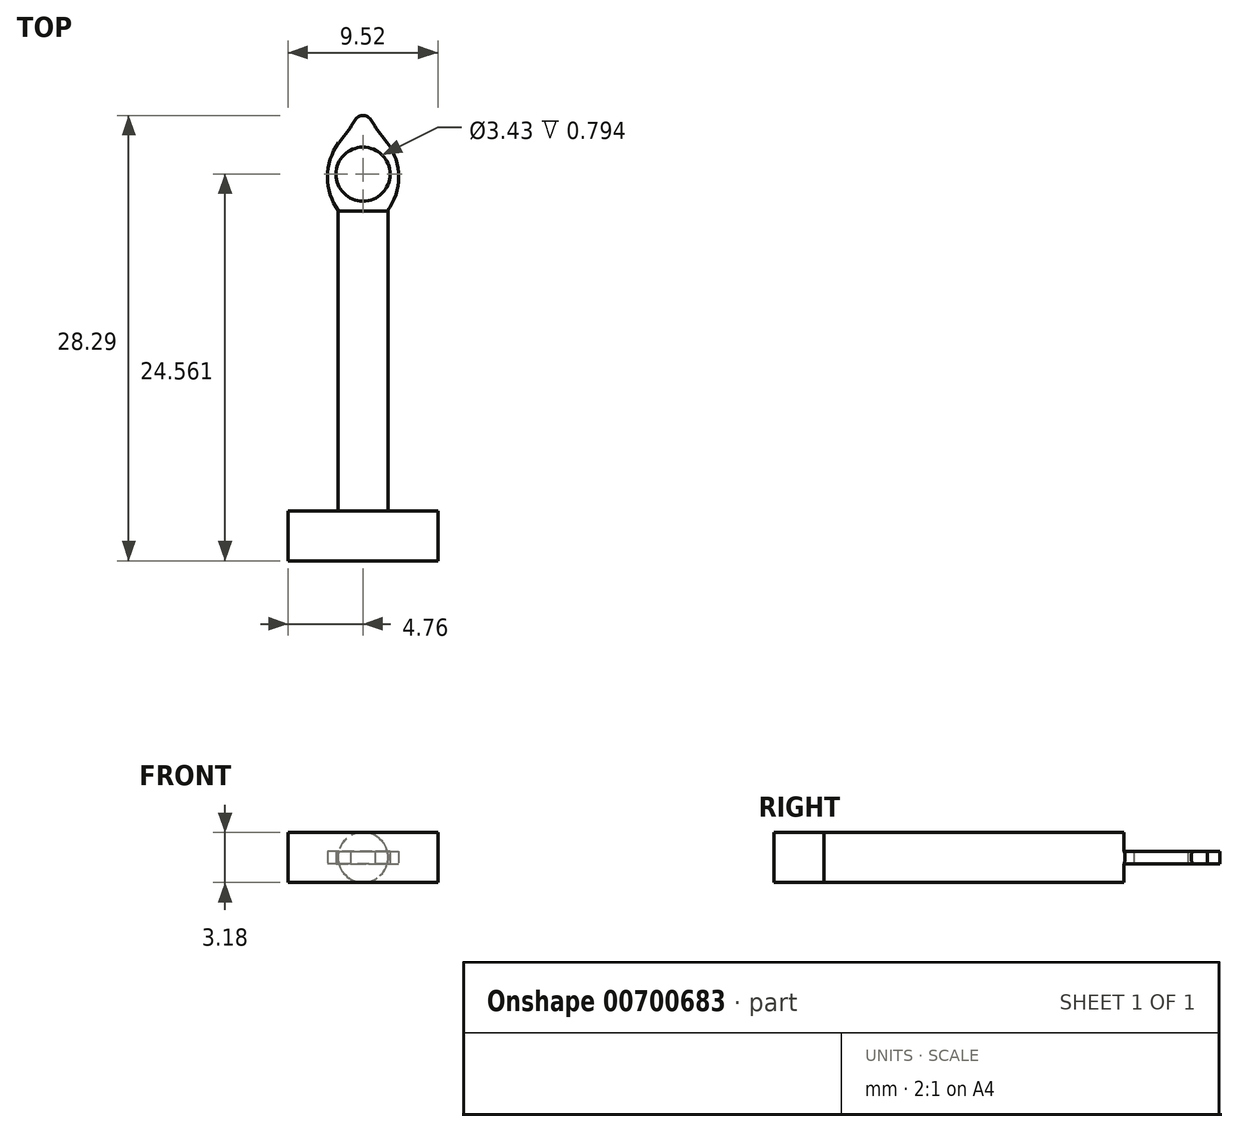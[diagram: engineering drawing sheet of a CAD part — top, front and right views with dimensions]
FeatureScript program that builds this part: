
annotation { "Feature Type Name" : "Feature", "Feature Type Description" : "" }
export const myFeature = defineFeature(function(context is Context, id is Id, definition is map)
    precondition{}
    {
        {
            var Q0;
            Q0=qCreatedBy(makeId("Front.planeOp"),FACE);
            var sketch = newSketch(context, id + "F0", { "sketchPlane" : qUnion([Q0])});
            skCircle(sketch, "E0", {"center": v(0, 0) * mm, "radius": 1.59 * mm});
            skSolve(sketch);
        }
        {
            var Q0;
            Q0 = qSketchRegion(id + "F0", true);
            extrude(context, id + "F1", {"entities" : qUnion([Q0]), "depth" : 25.4 * mm, "offsetDistance" : 25.4 * mm});
        }
        {
            var Q0;
            Q0=makeQuery(id+"F1.opExtrude","CAP_FACE",FACE,{"disambiguationData":[OSD([sQuery(id+"F0.wireOp",EDGE,"E0")])],"isStart":false});
            var sketch = newSketch(context, id + "F2", { "sketchPlane" : qUnion([Q0])});
            skLineSegment(sketch, "E1.bottom", {"start": v(-4.76, 1.59) * mm, "end": v(4.76, 1.59) * mm});
            skLineSegment(sketch, "E1.top", {"start": v(-4.76, -1.59) * mm, "end": v(4.76, -1.59) * mm});
            skLineSegment(sketch, "E1.left", {"start": v(-4.76, 1.59) * mm, "end": v(-4.76, -1.59) * mm});
            skLineSegment(sketch, "E1.right", {"start": v(4.76, 1.59) * mm, "end": v(4.76, -1.59) * mm});
            skPoint(sketch, "E2", {"position": v(0, 1.59) * mm});
            skPoint(sketch, "E3", {"position": v(0, -1.59) * mm});
            skSolve(sketch);
        }
        {
            var Q0;
            Q0 = qSketchRegion(id + "F2", true);
            extrude(context, id + "F3", {"entities" : qUnion([Q0]), "operationType" : NewBodyOperationType.ADD, "depth" : 3.17 * mm, "offsetDistance" : 25.4 * mm});
        }
        {
            var Q0;
            Q0=makeQuery(id+"F1.opExtrude","CAP_FACE",FACE,{"disambiguationData":[OSD([sQuery(id+"F0.wireOp",EDGE,"E0")])],"isStart":true});
            var sketch = newSketch(context, id + "F4", { "sketchPlane" : qUnion([Q0])});
            skLineSegment(sketch, "E4", {"start": v(1.54, 0.4) * mm, "end": v(-1.54, 0.4) * mm});
            skLineSegment(sketch, "E5", {"start": v(-1.54, -0.4) * mm, "end": v(1.54, -0.4) * mm});
            skArc(sketch, "E6.0", {"start": v(1.54, 0.4) * mm, "mid": v(0, 1.59) * mm, "end": v(-1.54, 0.4) * mm});
            skArc(sketch, "E7.trimOffspring", {"start": v(-1.54, -0.4) * mm, "mid": v(0, -1.59) * mm, "end": v(1.54, -0.4) * mm});
            skSolve(sketch);
        }
        {
            var Q0;
            Q0 = qSketchRegion(id + "F4", true);
            extrude(context, id + "F5", {"entities" : qUnion([Q0]), "operationType" : NewBodyOperationType.REMOVE, "oppositeDirection" : true, "depth" : 6.35 * mm, "offsetDistance" : 25.4 * mm});
        }
        {
            var Q0;
            Q0=makeQuery(id+"F5.boolean.opBoolean","COPY",FACE,{"derivedFrom":makeQuery(id+"F5.opExtrude","SWEPT_FACE",FACE,{"disambiguationData":[OSD([sQuery(id+"F4.wireOp",EDGE,"E5")])]})});
            var sketch = newSketch(context, id + "F6", { "sketchPlane" : qUnion([Q0])});
            skPoint(sketch, "E8", {"position": v(1.54, 2.02) * mm});
            skPoint(sketch, "E9", {"position": v(-1.54, 2.02) * mm});
            skLineSegment(sketch, "E10", {"start": v(0, 0) * mm, "end": v(1.54, 2.02) * mm});
            skLineSegment(sketch, "E11", {"start": v(0, 0) * mm, "end": v(-1.54, 2.02) * mm});
            skLineSegment(sketch, "E12", {"start": v(1.54, 2.02) * mm, "end": v(2.9, 3.82) * mm});
            skLineSegment(sketch, "E13", {"start": v(-1.54, 2.02) * mm, "end": v(-2.9, 3.82) * mm});
            skLineSegment(sketch, "E14", {"start": v(-2.9, 3.82) * mm, "end": v(-2.9, -0.78) * mm});
            skLineSegment(sketch, "E15", {"start": v(-2.9, -0.78) * mm, "end": v(2.9, -0.78) * mm});
            skLineSegment(sketch, "E16", {"start": v(2.9, -0.78) * mm, "end": v(2.9, 3.82) * mm});
            skSolve(sketch);
        }
        {
            var Q0;
            Q0 = qSketchRegion(id + "F6", true);
            extrude(context, id + "F7", {"entities" : qUnion([Q0]), "operationType" : NewBodyOperationType.REMOVE, "oppositeDirection" : true, "depth" : 25.4 * mm, "offsetDistance" : 25.4 * mm});
        }
        {
            var Q0;
            Q0=makeQuery(id+"F7.boolean.opBoolean","COPY",EDGE,{"derivedFrom":makeQuery(id+"F7.opExtrude","SWEPT_EDGE",EDGE,{"disambiguationData":[OSD([sQuery(id+"F4.wireOp",EDGE,"E5"),sQuery(id+"F6.wireOp",EDGE,"E10"),sQuery(id+"F6.wireOp",EDGE,"E11")])]})});
            fillet(context, id + "F8", {"entities" : qUnion([Q0]), "radius" : 1.02 * mm, "tangentPropagation" : true, "rho" : 0.5, "crossSection" : FilletCrossSection.CONIC, "allowEdgeOverflow" : false});
        }
        {
            var Q0;
            Q0=makeQuery(id+"F5.boolean.opBoolean","COPY",FACE,{"derivedFrom":makeQuery(id+"F5.opExtrude","SWEPT_FACE",FACE,{"disambiguationData":[OSD([sQuery(id+"F4.wireOp",EDGE,"E5")])]})});
            var sketch = newSketch(context, id + "F9", { "sketchPlane" : qUnion([Q0])});
            skFitSpline(sketch, "E17.0", {"points": [v(-0.8, 1.06) * mm, v(-0.27, 0.35) * mm, v(0.27, 0.35) * mm, v(0.8, 1.06) * mm]});
            skLineSegment(sketch, "E18.0", {"start": v(-0.8, 1.06) * mm, "end": v(-1.54, 2.02) * mm});
            skLineSegment(sketch, "E19.0", {"start": v(0.8, 1.06) * mm, "end": v(1.54, 2.02) * mm});
            skArc(sketch, "E20", {"start": v(1.54, 2.02) * mm, "mid": v(2.27, 4.18) * mm, "end": v(1.54, 6.35) * mm});
            skArc(sketch, "E21", {"start": v(-1.54, 6.35) * mm, "mid": v(-2.27, 4.18) * mm, "end": v(-1.54, 2.02) * mm});
            skLineSegment(sketch, "E22", {"start": v(1.54, 6.35) * mm, "end": v(-1.54, 6.35) * mm});
            skSolve(sketch);
        }
        {
            var Q0;
            Q0 = qSketchRegion(id + "F9", true);
            extrude(context, id + "F10", {"entities" : qUnion([Q0]), "operationType" : NewBodyOperationType.ADD, "oppositeDirection" : true, "depth" : 0.8 * mm, "offsetDistance" : 25.4 * mm});
        }
        {
            var Q0;
            Q0=makeQuery(id+"F10.boolean.opBoolean","MERGE",FACE,{"derivedFrom":[makeQuery(id+"F5.boolean.opBoolean","COPY",FACE,{"derivedFrom":makeQuery(id+"F5.opExtrude","SWEPT_FACE",FACE,{"disambiguationData":[OSD([sQuery(id+"F4.wireOp",EDGE,"E5")])]})}),makeQuery(id+"F10.opExtrude","CAP_FACE",FACE,{"disambiguationData":[OSD([sQuery(id+"F9.wireOp",EDGE,"E17.0"),sQuery(id+"F9.wireOp",EDGE,"E18.0"),sQuery(id+"F9.wireOp",EDGE,"E19.0"),sQuery(id+"F9.wireOp",EDGE,"E20"),sQuery(id+"F9.wireOp",EDGE,"E21"),sQuery(id+"F9.wireOp",EDGE,"E22")])],"isStart":true})]});
            var sketch = newSketch(context, id + "F11", { "sketchPlane" : qUnion([Q0])});
            skCircle(sketch, "E23", {"center": v(0, 4) * mm, "radius": 1.71 * mm});
            skSolve(sketch);
        }
        {
            var Q0;
            Q0 = qSketchRegion(id + "F11", true);
            extrude(context, id + "F12", {"entities" : qUnion([Q0]), "operationType" : NewBodyOperationType.REMOVE, "oppositeDirection" : true, "depth" : 25.4 * mm, "offsetDistance" : 25.4 * mm});
        }
    });
